# Revit family: РИДАН_Краны шаровые чугунные полнопроходные КШЧ
name_source: partatom
category: Арматура трубопроводов
units: mm (PartAtom-declared; Revit-internal decimal feet)

## family parameters
Всегда вертикально = Да
На основе рабочей плоскости = Нет
Общий = Нет
При загрузке вырезать с полостями = Нет
Размер круглого соединителя = Использовать диаметр
Тип детали = Вставляется

## types (12) — shared parameters
ADSK_Версия Revit = 2019
ADSK_Версия семейства = 1.0
ADSK_Единица измерения = шт.
ADSK_Завод-изготовитель = ООО «Ридан-Трейд»
ADSK_Количество = 1
LT = КШЧ
URL = https://ridan.ru
Изготовитель = ООО «Ридан-Трейд»

## per-type parameters (varying)
| type | ADSK_Диаметр условный | ADSK_Код изделия | ADSK_Марка | ADSK_Масса | ADSK_Наименование | a | a1 | b | b1 | c | c1 | d | d1 | e | e1 | e11 | f | f1 | g | g1 | h |
| DN 15 | 15 мм | 082X4800R | КШЧ DN15 | 2.68 | Кран шаровой КШЧ чугунный фланцевый, полнопроходный PN16, Tmax=150C, DN15 | 2 мм | 95 мм | 12 мм | 45 мм | 20 мм | 41 мм | 31 мм | 40 мм | 6 мм | 25 мм | 13 мм | 30 мм | 212 мм | 35 мм | 56 мм | 131 мм |
| DN 20 | 20 мм | 082X4801R | КШЧ DN20 | 4.1 | Кран шаровой КШЧ чугунный фланцевый, полнопроходный PN16, Tmax=150C, DN20 | 2 мм | 105 мм | 14 мм | 55 мм | 15 мм | 51 мм | 44 мм | 43 мм | 9 мм | 32 мм | 16 мм | 36 мм | 246 мм | 70 мм | 68 мм | 151 мм |
| DN 25 | 25 мм | 082X4802R | КШЧ DN25 | 5 | Кран шаровой КШЧ чугунный фланцевый, полнопроходный PN16, Tmax=150C, DN25 | 2 мм | 115 мм | 14 мм | 65 мм | 15 мм | 61 мм | 49 мм | 50 мм | 17 мм | 37 мм | 19 мм | 36 мм | 231 мм | 64 мм | 75 мм | 160 мм |
| DN 32 | 32 мм | 082X4803R | КШЧ DN32 | 6.3 | Кран шаровой КШЧ чугунный фланцевый, полнопроходный PN16, Tmax=150C, DN32 | 2 мм | 135 мм | 15 мм | 78 мм | 18 мм | 74 мм | 48 мм | 61 мм | 14 мм | 46 мм | 23 мм | 36 мм | 220 мм | 59 мм | 78 мм | 165 мм |
| DN 40 | 40 мм | 082X4804R | КШЧ DN40 | 7.73 | Кран шаровой КШЧ чугунный фланцевый, полнопроходный PN16, Tmax=120C, DN40 | 3 мм | 150 мм | 15 мм | 88 мм | 15 мм | 82 мм | 38 мм | 84 мм | 15 мм | 54 мм | 27 мм | 50 мм | 202 мм | 43 мм | 101 мм | 140 мм |
| DN 50 | 50 мм | 082X4805R | КШЧ DN50 | 9.82 | Кран шаровой КШЧ чугунный фланцевый, полнопроходный PN16, Tmax=120C, DN50 | 3 мм | 165 мм | 17 мм | 102 мм | 16 мм | 96 мм | 38 мм | 94 мм | 13 мм | 64 мм | 32 мм | 50 мм | 193 мм | 41 мм | 114 мм | 147 мм |
| DN 65 | 65 мм | 082X4806R | КШЧ DN65 | 13.98 | Кран шаровой КШЧ чугунный фланцевый, полнопроходный PN16, Tmax=120C, DN65 | 3 мм | 185 мм | 17 мм | 122 мм | 8 мм | 116 мм | 55 мм | 116 мм | 6 мм | 100 мм | 50 мм | 54 мм | 230 мм | 90 мм | 135 мм | 167 мм |
| DN 80 | 80 мм | 082X4807R | КШЧ DN80 | 17.2 | Кран шаровой КШЧ чугунный фланцевый, полнопроходный PN16, Tmax=120C, DN80 | 3 мм | 200 мм | 19 мм | 138 мм | 7 мм | 132 мм | 60 мм | 129 мм | 5 мм | 116 мм | 58 мм | 58 мм | 241 мм | 108 мм | 141 мм | 177 мм |
| DN 100 | 100 мм | 082X4808R | КШЧ DN100 | 24.26 | Кран шаровой КШЧ чугунный фланцевый, полнопроходный PN16, Tmax=120C, DN100 | 3 мм | 220 мм | 21 мм | 158 мм | 7 мм | 152 мм | 64 мм | 150 мм | 2 мм | 140 мм | 70 мм | 58 мм | 214 мм | 99 мм | 155 мм | 190 мм |
| DN 125 | 125 мм | 082X4809R | КШЧ DN125 | 40.2 | Кран шаровой КШЧ чугунный фланцевый, полнопроходный PN16, Tmax=120C, DN125 | 3 мм | 250 мм | 23 мм | 188 мм | 34 мм | 182 мм | 103 мм | 183 мм | 0 мм | 147 мм | 74 мм | 70 мм | 236 мм | 144 мм | 186 мм | 325 мм |
| DN 150 | 150 мм | 082X4810R | КШЧ DN150 | 54.65 | Кран шаровой КШЧ чугунный фланцевый, полнопроходный PN16, Tmax=120C, DN150 | 3 мм | 285 мм | 23 мм | 211 мм | 23 мм | 205 мм | 126 мм | 237 мм | 0 мм | 176 мм | 88 мм | 78 мм | 236 мм | 171 мм | 199 мм | 350 мм |
| DN 200 | 200 мм | 082X4811R | КШЧ DN200 | 100.1 | Кран шаровой КШЧ чугунный фланцевый, полнопроходный PN16, Tmax=120C, DN200 | 3 мм | 340 мм | 27 мм | 266 мм | 27 мм | 260 мм | 143 мм | 254 мм | 0 мм | 229 мм | 115 мм | 82 мм | 237 мм | 206 мм | 261 мм | 400 мм |
